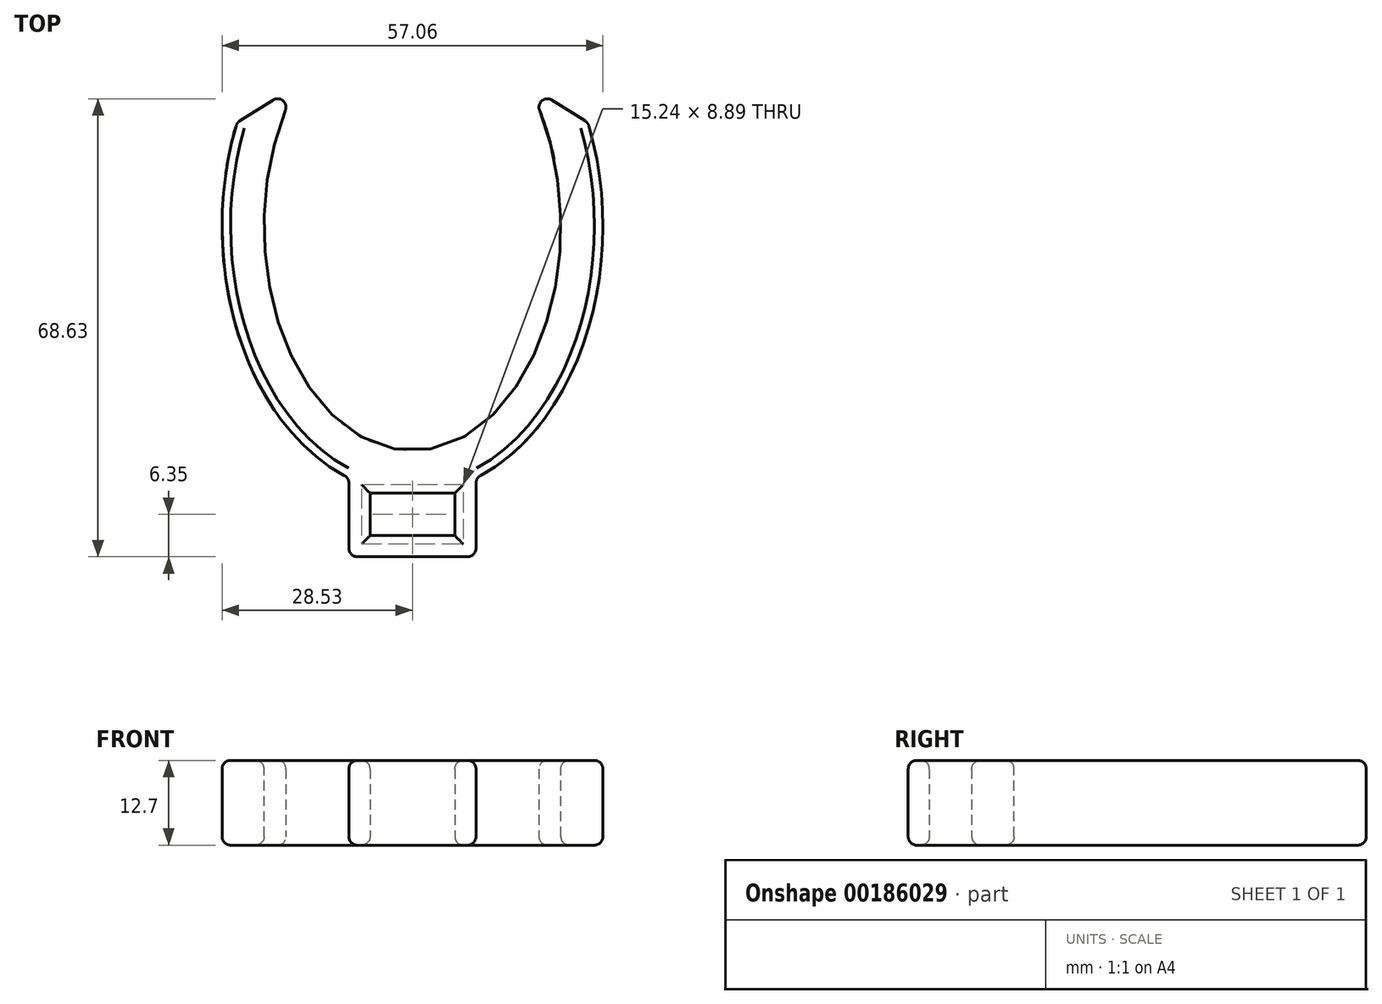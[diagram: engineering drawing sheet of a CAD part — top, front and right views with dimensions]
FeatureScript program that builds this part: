
annotation { "Feature Type Name" : "Feature", "Feature Type Description" : "" }
export const myFeature = defineFeature(function(context is Context, id is Id, definition is map)
    precondition{}
    {
        {
            var Q0;
            Q0=qCreatedBy(makeId("Top.planeOp"),FACE);
            var sketch = newSketch(context, id + "F0", { "sketchPlane" : qUnion([Q0])});
            skLineSegment(sketch, "E0", {"start": v(-26.3, 15.49) * mm, "end": v(-17.26, 21.2) * mm});
            skLineSegment(sketch, "E1.MirrorCS", {"start": v(26.3, 15.49) * mm, "end": v(17.26, 21.2) * mm});
            skEllipticalArc(sketch, "E2", {});
            skEllipticalArc(sketch, "E3", {});
            skEllipse(sketch, "E4", {"center": v(0, 0) * mm, "majorRadius": 28.53 * mm, "minorRadius": 40 * mm, "majorAxis": v(1, 0)});
            skLineSegment(sketch, "E5.bottom", {"start": v(6.35, -40) * mm, "end": v(-6.35, -40) * mm});
            skLineSegment(sketch, "E5.top", {"start": v(6.35, -46.36) * mm, "end": v(-6.35, -46.36) * mm});
            skLineSegment(sketch, "E5.left", {"start": v(6.35, -40) * mm, "end": v(6.35, -46.36) * mm});
            skLineSegment(sketch, "E5.right", {"start": v(-6.35, -40) * mm, "end": v(-6.35, -46.36) * mm});
            skPoint(sketch, "E5.middle", {"position": v(0, -43.18) * mm});
            skPoint(sketch, "E6", {"position": v(0, -40) * mm});
            skLineSegment(sketch, "E7.0", {"start": v(-9.53, -40.93) * mm, "end": v(-9.52, -49.53) * mm});
            skLineSegment(sketch, "E7.1", {"start": v(9.53, -49.53) * mm, "end": v(-9.52, -49.53) * mm});
            skLineSegment(sketch, "E7.2", {"start": v(9.53, -40.93) * mm, "end": v(9.53, -49.53) * mm});
            skLineSegment(sketch, "E8", {"start": v(-9.53, -40.93) * mm, "end": v(-9.53, -37.7) * mm});
            skLineSegment(sketch, "E9", {"start": v(9.52, -40.93) * mm, "end": v(9.52, -37.7) * mm});
            const initialGuessF0  = {"E2": [0, 0, 1, 0, 0.022225, 0.033655, 2.460227135916155, 0.6813655176736377], "E3": [0, 0, 1, 0, 0.022225406909298712, 0.033654063049122454, 0.6813880944836717, 2.4602045591061206]};
            skSetInitialGuess(sketch, initialGuessF0);
            skSolve(sketch);
        }
        {
            var Q0;
            Q0=makeQuery(id+"F0.imprint","IMPRINT",FACE,{"disambiguationData":[TD([[makeQuery(id+"F0.imprint","IMPRINT",EDGE,{"derivedFrom":sQuery(id+"F0.wireOp",EDGE,"E5.top")}),1.0]])]});
            var Q1;
            {var subQ1=sQuery(id+"F0.wireOp",EDGE,"E0");Q1=makeQuery(id+"F0.imprint","IMPRINT",FACE,{"disambiguationData":[TD([[makeQuery(id+"F0.imprint","IMPRINT",EDGE,{"derivedFrom":subQ1}),-1.0]])]});}
            extrude(context, id + "F1", {"entities" : qUnion([Q0, Q1]), "depth" : 12.7 * mm});
        }
        {
            var Q0;
            Q0=makeQuery(id+"F1.opExtrude","CAP_FACE",FACE,{"disambiguationData":[OSD([sQuery(id+"F0.wireOp",EDGE,"E0"),sQuery(id+"F0.wireOp",EDGE,"E1.MirrorCS"),sQuery(id+"F0.wireOp",EDGE,"E2"),sQuery(id+"F0.wireOp",EDGE,"E4"),sQuery(id+"F0.wireOp",EDGE,"E5.bottom"),sQuery(id+"F0.wireOp",EDGE,"E5.top"),sQuery(id+"F0.wireOp",EDGE,"E5.left"),sQuery(id+"F0.wireOp",EDGE,"E5.right"),sQuery(id+"F0.wireOp",EDGE,"E7.0"),sQuery(id+"F0.wireOp",EDGE,"E7.1"),sQuery(id+"F0.wireOp",EDGE,"E7.2"),sQuery(id+"F0.wireOp",EDGE,"E8"),sQuery(id+"F0.wireOp",EDGE,"E9")])],"isStart":false});
            var Q1;
            Q1=makeQuery(id+"F1.opExtrude","CAP_FACE",FACE,{"disambiguationData":[OSD([sQuery(id+"F0.wireOp",EDGE,"E0"),sQuery(id+"F0.wireOp",EDGE,"E1.MirrorCS"),sQuery(id+"F0.wireOp",EDGE,"E2"),sQuery(id+"F0.wireOp",EDGE,"E4"),sQuery(id+"F0.wireOp",EDGE,"E5.bottom"),sQuery(id+"F0.wireOp",EDGE,"E5.top"),sQuery(id+"F0.wireOp",EDGE,"E5.left"),sQuery(id+"F0.wireOp",EDGE,"E5.right"),sQuery(id+"F0.wireOp",EDGE,"E7.0"),sQuery(id+"F0.wireOp",EDGE,"E7.1"),sQuery(id+"F0.wireOp",EDGE,"E7.2"),sQuery(id+"F0.wireOp",EDGE,"E8"),sQuery(id+"F0.wireOp",EDGE,"E9")])],"isStart":true});
            var Q2;
            {var subQ0=sQuery(id+"F0.wireOp",EDGE,"E4");Q2=makeQuery(id+"F1.opExtrude","SWEPT_FACE",FACE,{"disambiguationData":[OSD([subQ0]),TDD([makeQuery(id+"F0.imprint","IMPRINT",EDGE,{"disambiguationData":[TD([[makeQuery(id+"F0.imprint","INTERSECT",VERTEX,{"derivedFrom":[sQuery(id+"F0.wireOp",EDGE,"E0"),subQ0]}),-1.0]])],"derivedFrom":subQ0})])]});}
            var Q3;
            Q3=makeQuery(id+"F1.opExtrude","SWEPT_FACE",FACE,{"disambiguationData":[OSD([sQuery(id+"F0.wireOp",EDGE,"E7.1")])]});
            var Q4;
            {var subQ0=sQuery(id+"F0.wireOp",EDGE,"E4");Q4=makeQuery(id+"F1.opExtrude","SWEPT_FACE",FACE,{"disambiguationData":[OSD([subQ0]),TDD([makeQuery(id+"F0.imprint","IMPRINT",EDGE,{"disambiguationData":[TD([[makeQuery(id+"F0.imprint","INTERSECT",VERTEX,{"derivedFrom":[sQuery(id+"F0.wireOp",EDGE,"E1.MirrorCS"),subQ0]}),1.0]])],"derivedFrom":subQ0})])]});}
            var Q5;
            Q5=makeQuery(id+"F1.opExtrude","SWEPT_FACE",FACE,{"disambiguationData":[OSD([sQuery(id+"F0.wireOp",EDGE,"E2")])]});
            fillet(context, id + "F2", {"entities" : qUnion([Q0, Q1, Q2, Q3, Q4, Q5]), "radius" : 1.27 * mm, "tangentPropagation" : true, "allowEdgeOverflow" : false});
        }
    });
